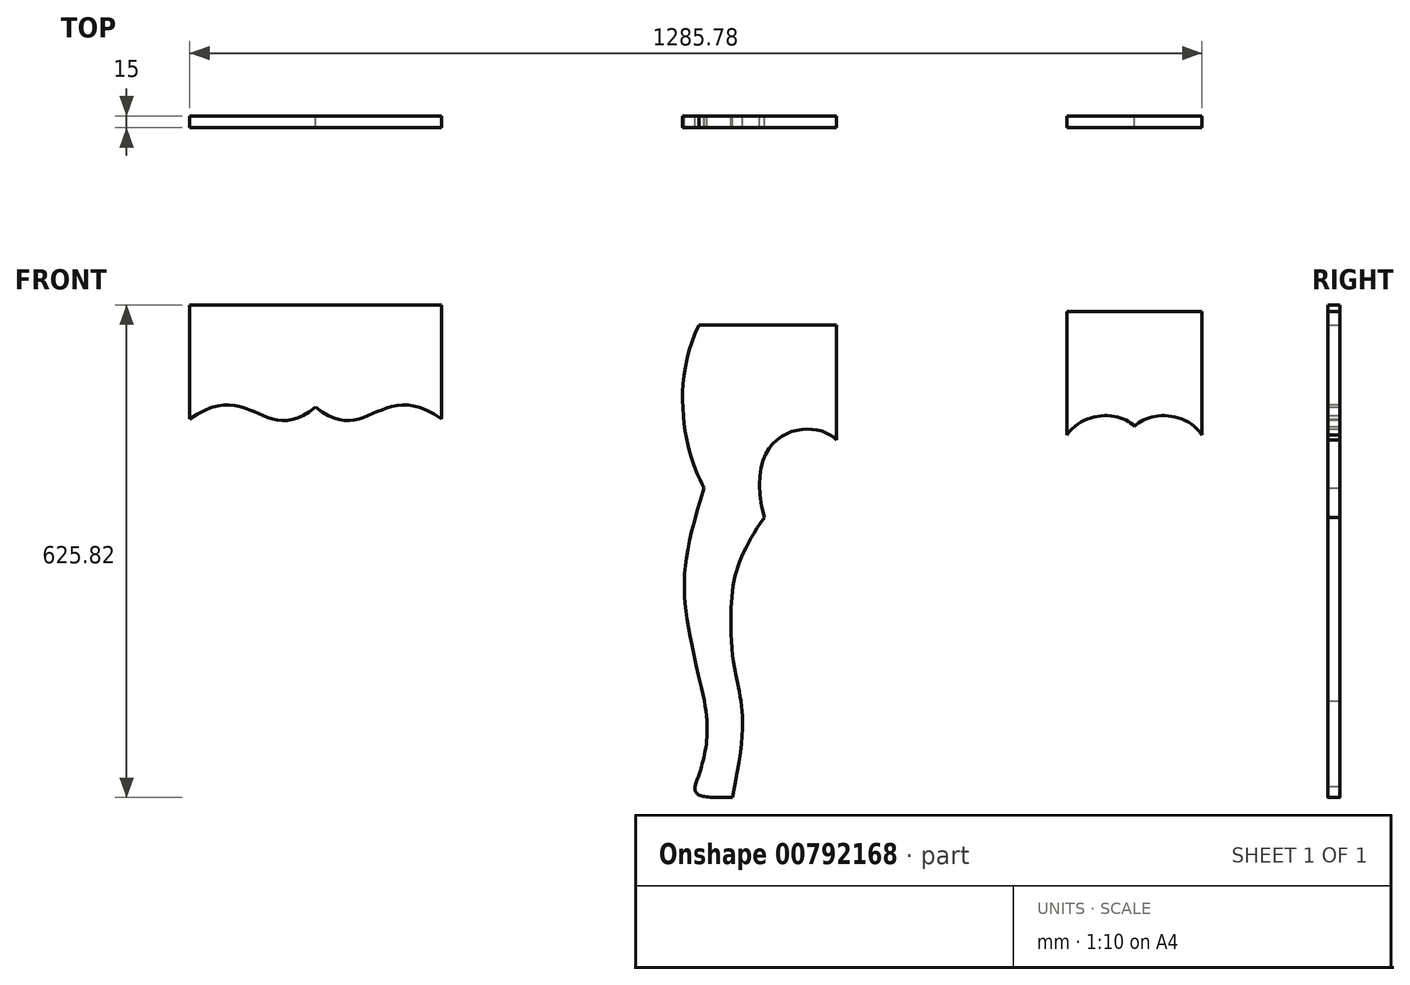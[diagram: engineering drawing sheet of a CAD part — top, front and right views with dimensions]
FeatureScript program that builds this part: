
annotation { "Feature Type Name" : "Feature", "Feature Type Description" : "" }
export const myFeature = defineFeature(function(context is Context, id is Id, definition is map)
    precondition{}
    {
        {
            var Q0;
            Q0=qCreatedBy(makeId("Front.planeOp"),FACE);
            var sketch = newSketch(context, id + "F0", { "sketchPlane" : qUnion([Q0])});
            skFitSpline(sketch, "E0", {"points": [v(288.11, 255.17) * mm, v(294.97, 48.6) * mm], "startDerivative": vector(-116.75, -242.74) * mm, "endDerivative": vector(63.83, -108.67) * mm});
            skFitSpline(sketch, "E1", {"points": [v(294.97, 48.6) * mm, v(295.17, -221.83) * mm], "startDerivative": vector(-114.72, -365.12) * mm, "endDerivative": vector(87.28, -386.33) * mm});
            skFitSpline(sketch, "E2", {"points": [v(295.17, -221.83) * mm, v(283.45, -330.8) * mm], "startDerivative": vector(27.3, -157.52) * mm, "endDerivative": vector(-31.55, -99.56) * mm});
            skFitSpline(sketch, "E3", {"points": [v(283.45, -330.8) * mm, v(330.83, -344.83) * mm], "startDerivative": vector(-6.63, -45.66) * mm, "endDerivative": vector(96.5, -0.1) * mm});
            skFitSpline(sketch, "E4", {"points": [v(330.83, -344.83) * mm, v(329.66, -145.85) * mm], "startDerivative": vector(82.15, 395.38) * mm, "endDerivative": vector(-12.75, 233.9) * mm});
            skFitSpline(sketch, "E5", {"points": [v(329.66, -145.85) * mm, v(371.42, 10.75) * mm], "startDerivative": vector(-10.77, 215.46) * mm, "endDerivative": vector(112.62, 159.55) * mm});
            skFitSpline(sketch, "E6", {"points": [v(371.42, 10.75) * mm, v(463.11, 109.54) * mm], "startDerivative": vector(-93.37, 361) * mm, "endDerivative": vector(75.96, -83.28) * mm});
            skLineSegment(sketch, "E7", {"start": v(288.11, 255.17) * mm, "end": v(463.11, 255.17) * mm});
            skLineSegment(sketch, "E8", {"start": v(463.11, 255.17) * mm, "end": v(463.11, 109.54) * mm});
            skLineSegment(sketch, "E9", {"start": v(756.06, 272.26) * mm, "end": v(756.06, 115.84) * mm});
            skFitSpline(sketch, "E10", {"points": [v(749.97, 27.84) * mm, v(841.67, 126.63) * mm], "startDerivative": vector(-93.37, 361) * mm, "endDerivative": vector(75.96, -83.28) * mm});
            skLineSegment(sketch, "E11.MirrorCS", {"start": v(927.28, 272.26) * mm, "end": v(927.28, 115.84) * mm});
            skFitSpline(sketch, "E12.MirrorCS", {"points": [v(933.36, 27.84) * mm, v(841.67, 126.63) * mm], "startDerivative": vector(93.37, 361) * mm, "endDerivative": vector(-75.96, -83.28) * mm});
            skLineSegment(sketch, "E13", {"start": v(756.06, 272.26) * mm, "end": v(927.28, 272.26) * mm});
            skLineSegment(sketch, "E14.MirrorCS", {"start": v(-38.5, 280.98) * mm, "end": v(-38.5, 135.98) * mm});
            skLineSegment(sketch, "E15", {"start": v(-198.5, 280.98) * mm, "end": v(-38.5, 280.98) * mm});
            skPoint(sketch, "E16", {"position": v(-198.5, 151.2) * mm});
            skFitSpline(sketch, "E17", {"points": [v(-198.5, 151.2) * mm, v(-38.5, 135.98) * mm], "startDerivative": vector(193.15, -158.81) * mm, "endDerivative": vector(230.3, -162.64) * mm});
            skLineSegment(sketch, "E18", {"start": v(-198.5, 280.98) * mm, "end": v(-198.5, 151.2) * mm});
            skLineSegment(sketch, "E19.MirrorCS", {"start": v(-358.5, 280.98) * mm, "end": v(-358.5, 135.98) * mm});
            skFitSpline(sketch, "E20.MirrorCS", {"points": [v(-198.5, 151.2) * mm, v(-358.5, 135.98) * mm], "startDerivative": vector(-193.15, -158.81) * mm, "endDerivative": vector(-230.3, -162.64) * mm});
            skLineSegment(sketch, "E21.MirrorCS", {"start": v(-198.5, 280.98) * mm, "end": v(-358.5, 280.98) * mm});
            skLineSegment(sketch, "E22", {"start": v(-38.5, 135.98) * mm, "end": v(-358.5, 135.98) * mm, "construction": true});
            skSolve(sketch);
        }
        {
            var Q0;
            Q0=makeQuery(id+"F0.imprint","IMPRINT",FACE,{"disambiguationData":[TD([[makeQuery(id+"F0.imprint","IMPRINT",EDGE,{"derivedFrom":sQuery(id+"F0.wireOp",EDGE,"E0")}),1.0]])]});
            extrude(context, id + "F1", {"entities" : qUnion([Q0]), "depth" : 15 * mm, "offsetDistance" : 25 * mm});
        }
        {
            var Q0;
            Q0=makeQuery(id+"F0.imprint","IMPRINT",FACE,{"disambiguationData":[TD([[makeQuery(id+"F0.imprint","IMPRINT",EDGE,{"derivedFrom":sQuery(id+"F0.wireOp",EDGE,"E9")}),1.0]])]});
            extrude(context, id + "F2", {"entities" : qUnion([Q0]), "depth" : 15 * mm, "offsetDistance" : 25 * mm});
        }
        {
            var Q0;
            Q0=makeQuery(id+"F0.imprint","IMPRINT",FACE,{"disambiguationData":[TD([[makeQuery(id+"F0.imprint","IMPRINT",EDGE,{"derivedFrom":sQuery(id+"F0.wireOp",EDGE,"E18")}),-1.0]])]});
            var Q1;
            Q1=makeQuery(id+"F0.imprint","IMPRINT",FACE,{"disambiguationData":[TD([[makeQuery(id+"F0.imprint","IMPRINT",EDGE,{"derivedFrom":sQuery(id+"F0.wireOp",EDGE,"E14.MirrorCS")}),-1.0]])]});
            extrude(context, id + "F3", {"entities" : qUnion([Q0, Q1]), "depth" : 15 * mm, "offsetDistance" : 25 * mm});
        }
    });
